# Revit family: EKF_EE_МонтажнаяПлатаДляВертикальныхАвтоматическихВыключателейTrivia_AVERES
name_source: partatom
category: Электрооборудование
units: mm (PartAtom-declared; Revit-internal decimal feet)

## family parameters
Всегда вертикально = Нет
На основе рабочей плоскости = Да
Общий = Да
При загрузке вырезать с полостями = Нет
Размер круглого соединителя = Использовать диаметр
Тип детали = Силовой щит
Точка расчета площади = Нет

## types (11) — shared parameters
ADSK_Единица измерения = шт.
ADSK_Завод-изготовитель = EKF
ADSK_Количество = 1
ADSK_Материал = RAL 7035_Сталь
ADSK_Размер_Глубина = 18 мм
ADSK_Размер_Ширина = 515 мм
Изготовитель = EKF
Отметка по умолчанию = 1219.2 мм
Серия номенклатуры = Averes
Степень защиты IP = -
ТВ = EKF_2_TRIVIA_AVERES
Тип установки = -
Тип_Платы = Монтажная плата 1
zero-valued in all types: ADSK_Масса

## per-type parameters (varying)
| type | ADSK_Код изделия | ADSK_Марка | ADSK_Наименование | ADSK_Обозначение | ADSK_Размер_Высота | Тип |
| Монтажная плата для 3-х вертикальных AV POWER-3 TM/ETU 3P EKF AVERES | MPFU0901 | Монтажная плата для 3-х вертикальных AV POWER-3 TM/ETU 3P EKF AVERES | Монтажная плата для 3-х вертикальных AV POWER-3 TM/ETU 3P EKF AVERES | Монтажная плата для 3-х вертикальных AV POWER-3 TM/ETU 3P EKF AVERES | 275 мм | 531 мм |
| Монтажная плата для 4-х вертикальных AV POWER-1 TM 3P EKF AVERES | MPFU0601 | Монтажная плата для 4-х вертикальных AV POWER-1 TM 3P EKF AVERES | Монтажная плата для 4-х вертикальных AV POWER-1 TM 3P EKF AVERES | Монтажная плата для 4-х вертикальных AV POWER-1 TM 3P EKF AVERES | 148 мм | 532 мм |
| Монтажная плата для 4-х вертикальных AV POWER-2 TM/ETU 3P EKF AVERES | MPFU0801 | Монтажная плата для 4-х вертикальных AV POWER-2 TM/ETU 3P EKF AVERES | Монтажная плата для 4-х вертикальных AV POWER-2 TM/ETU 3P EKF AVERES | Монтажная плата для 4-х вертикальных AV POWER-2 TM/ETU 3P EKF AVERES | 187 мм | 533 мм |
| Монтажная плата для вертикального ВА-99/1600  3Р/4Р | MPFU6101 | Монтажная плата для вертикального ВА-99/1600 3Р/4Р | Монтажная плата для вертикального ВА-99/1600 3Р/4Р | Монтажная плата для вертикального ВА-99/1600 3Р/4Р | 450 мм | 534 мм |
| Монтажная плата для вертикальных ВА-99/125 4х3Р/3х4Р EKF AVERES | MPFU3101 | Монтажная плата для вертикальных ВА-99/125 4х3Р/3х4Р EKF AVERES | Монтажная плата для вертикальных ВА-99/125 4х3Р/3х4Р EKF AVERES | Монтажная плата для вертикальных ВА-99/125 4х3Р/3х4Р EKF AVERES | 148 мм | 535 мм |
| Монтажная плата для вертикальных ВА-99/160  4х3Р/3х4Р | MPFU3201 | Монтажная плата для вертикальных ВА-99/160 4х3Р/3х4Р | Монтажная плата для вертикальных ВА-99/160 4х3Р/3х4Р | Монтажная плата для вертикальных ВА-99/160 4х3Р/3х4Р | 148 мм | 536 мм |
| Монтажная плата для вертикальных ВА-99/250 3х3Р/3х4Р EKF AVERES | MPFU3301 | Монтажная плата для вертикальных ВА-99/250 3х3Р/3х4Р EKF AVERES | Монтажная плата для вертикальных ВА-99/250 3х3Р/3х4Р EKF AVERES | Монтажная плата для вертикальных ВА-99/250 3х3Р/3х4Р EKF AVERES | 187 мм | 537 мм |
| Монтажная плата для вертикальных ВА-99/400  3х3Р/2х4Р | MPFU3401 | Монтажная плата для вертикальных ВА-99/400 3х3Р/2х4Р | Монтажная плата для вертикальных ВА-99/400 3х3Р/2х4Р | Монтажная плата для вертикальных ВА-99/400 3х3Р/2х4Р | 255 мм | 538 мм |
| Монтажная плата для вертикальных ВА-99/800  1х3Р/1х4Р | MPFU3501 | Монтажная плата для вертикальных ВА-99/800 1х3Р/1х4Р | Монтажная плата для вертикальных ВА-99/800 1х3Р/1х4Р | Монтажная плата для вертикальных ВА-99/800 1х3Р/1х4Р | 275 мм | 539 мм |
| Монтажная плата для вертикальных ВА-99С/100/160/250 4х3Р/3х4Р EKF AVERES | MPFU6601 | Монтажная плата для вертикальных ВА-99С/100/160/250 4х3Р/3х4Р EKF AVERES | Монтажная плата для вертикальных ВА-99С/100/160/250 4х3Р/3х4Р EKF AVERES | Монтажная плата для вертикальных ВА-99С/100/160/250 4х3Р/3х4Р EKF AVERES | 187 мм | 540 мм |
| Монтажная плата для вертикальных ВА-99С/400/630 3х3Р/2х4Р EKF AVERES | MPFU6701 | Монтажная плата для вертикальных ВА-99С/400/630 3х3Р/2х4Р EKF AVERES | Монтажная плата для вертикальных ВА-99С/400/630 3х3Р/2х4Р EKF AVERES | Монтажная плата для вертикальных ВА-99С/400/630 3х3Р/2х4Р EKF AVERES | 275 мм | 541 мм |
